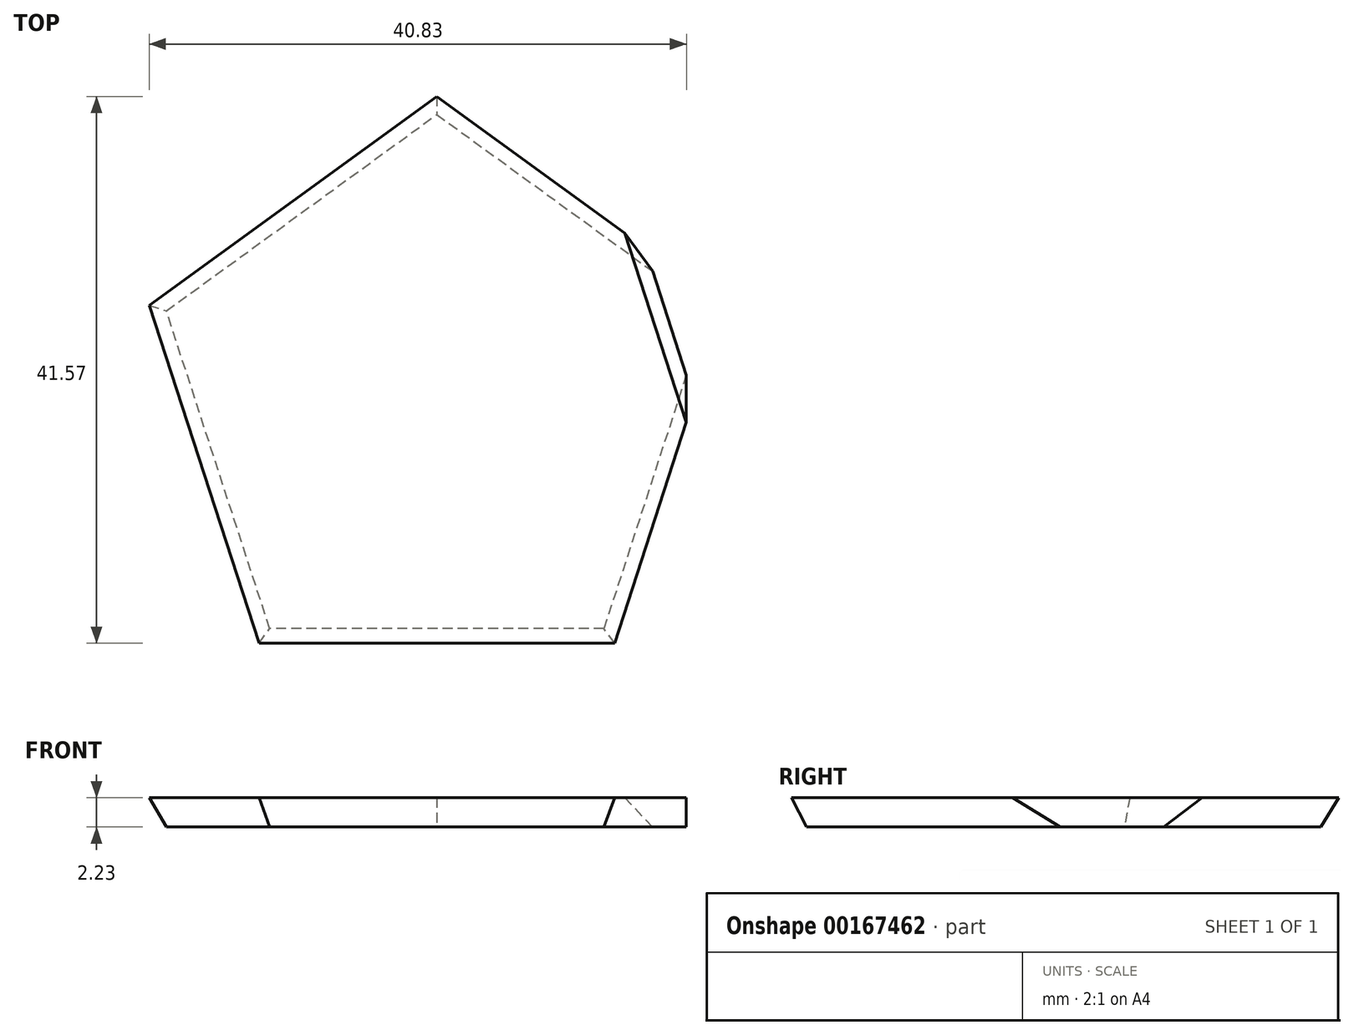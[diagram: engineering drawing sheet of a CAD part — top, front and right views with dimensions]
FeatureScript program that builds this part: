
annotation { "Feature Type Name" : "Feature", "Feature Type Description" : "" }
export const myFeature = defineFeature(function(context is Context, id is Id, definition is map)
    precondition{}
    {
        {
            var Q0;
            Q0=qCreatedBy(makeId("Top.planeOp"),FACE);
            var sketch = newSketch(context, id + "F0", { "sketchPlane" : qUnion([Q0])});
            skCircle(sketch, "E0.cCircle", {"center": v(0, 0) * mm, "radius": 17.48 * mm, "construction": true});
            skLineSegment(sketch, "E0.0", {"start": v(20.55, 6.68) * mm, "end": v(12.7, -17.48) * mm});
            skLineSegment(sketch, "E0.1", {"start": v(12.7, -17.48) * mm, "end": v(-12.7, -17.48) * mm});
            skLineSegment(sketch, "E0.2", {"start": v(-12.7, -17.48) * mm, "end": v(-20.55, 6.68) * mm});
            skLineSegment(sketch, "E0.3", {"start": v(-20.55, 6.68) * mm, "end": v(0, 21.6) * mm});
            skLineSegment(sketch, "E0.4", {"start": v(0, 21.6) * mm, "end": v(20.55, 6.68) * mm});
            skPoint(sketch, "E0.0.midPoint", {"position": v(16.62, -5.4) * mm});
            skSolve(sketch);
        }
        {
            var Q0;
            Q0=makeQuery(id+"F0.imprint","IMPRINT",FACE,{"disambiguationData":[TD([[makeQuery(id+"F0.imprint","IMPRINT",EDGE,{"derivedFrom":sQuery(id+"F0.wireOp",EDGE,"E0.0")}),-1.0]])]});
            var Q1;
            Q1 = qSketchRegion(id + "F2", true);
            extrude(context, id + "F1", {"entities" : qUnion([Q0, Q1]), "depth" : ((1 / sin(36 * degree)) * (sin(18 * degree) + 1)) * mm, "hasDraft" : true, "draftAngle" : acos(-1 / sqrt(5)) - 90 * degree});
        }
        {
            var Q0;
            Q0=makeQuery(id+"F1.opExtrude","CAP_FACE",FACE,{"disambiguationData":[OSD([sQuery(id+"F0.wireOp",EDGE,"E0.0"),sQuery(id+"F0.wireOp",EDGE,"E0.1"),sQuery(id+"F0.wireOp",EDGE,"E0.2"),sQuery(id+"F0.wireOp",EDGE,"E0.3"),sQuery(id+"F0.wireOp",EDGE,"E0.4")])],"isStart":false});
            var sketch = newSketch(context, id + "F2", { "sketchPlane" : qUnion([Q0])});
            skCircle(sketch, "E1.cCircle", {"center": v(0, 0) * mm, "radius": 17.48 * mm, "construction": true});
            skLineSegment(sketch, "E1.0", {"start": v(12.7, 17.48) * mm, "end": v(20.55, -6.68) * mm});
            skLineSegment(sketch, "E1.1", {"start": v(20.55, -6.68) * mm, "end": v(0, -21.6) * mm});
            skLineSegment(sketch, "E1.2", {"start": v(0, -21.6) * mm, "end": v(-20.55, -6.68) * mm});
            skLineSegment(sketch, "E1.3", {"start": v(-20.55, -6.68) * mm, "end": v(-12.7, 17.48) * mm});
            skLineSegment(sketch, "E1.4", {"start": v(-12.7, 17.48) * mm, "end": v(12.7, 17.48) * mm});
            skPoint(sketch, "E1.0.midPoint", {"position": v(16.62, 5.4) * mm});
            skSolve(sketch);
        }
        {
            var Q0;
            Q0=makeQuery(id+"F2.imprint","IMPRINT",FACE,{"disambiguationData":[TD([[makeQuery(id+"F2.imprint","IMPRINT",EDGE,{"derivedFrom":sQuery(id+"F2.wireOp",EDGE,"E1.0")}),1.0]])]});
            extrude(context, id + "F3", {"entities" : qUnion([Q0]), "operationType" : NewBodyOperationType.REMOVE, "oppositeDirection" : true, "depth" : 69.6 * mm, "hasDraft" : true, "draftAngle" : acos(-1 / sqrt(5)) - 90 * degree, "draftPullDirection" : true});
        }
    });
